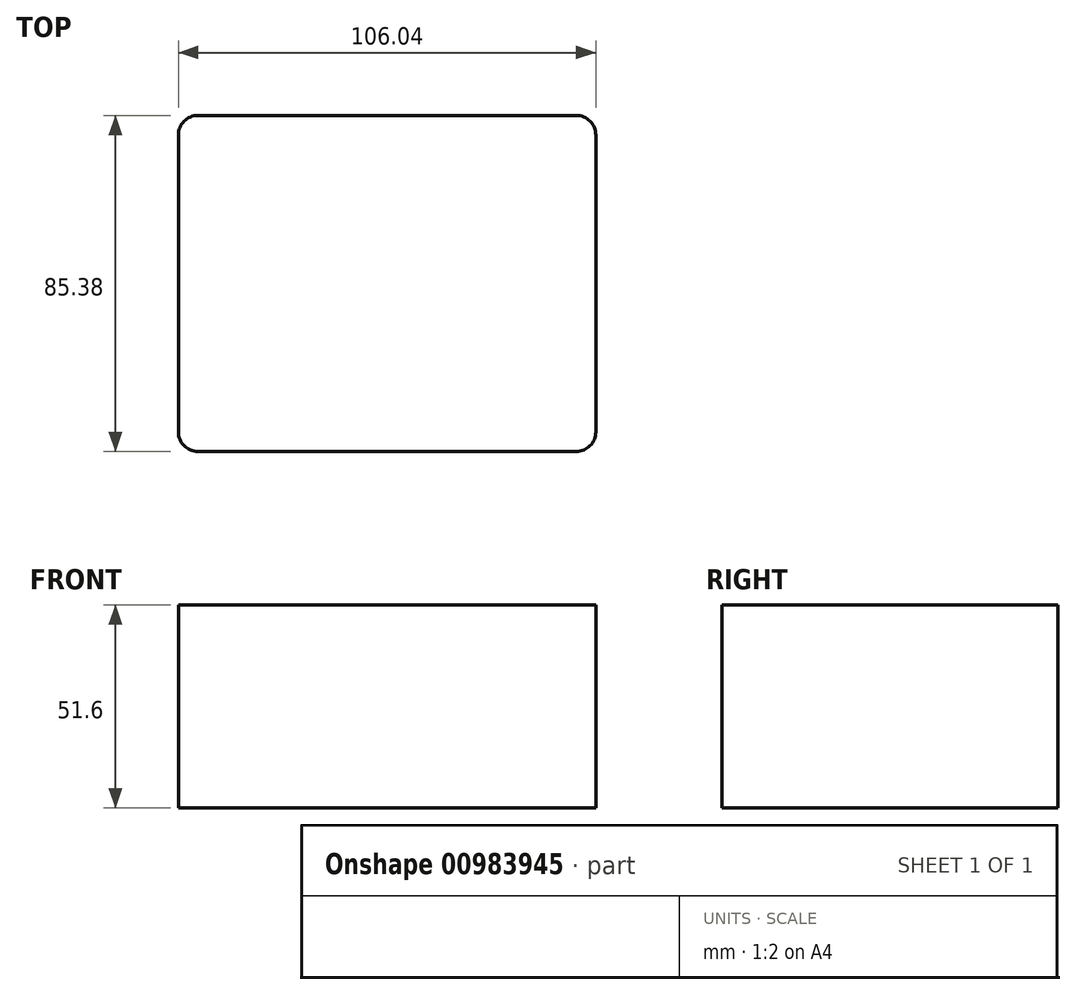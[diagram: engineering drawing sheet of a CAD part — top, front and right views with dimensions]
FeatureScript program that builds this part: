
annotation { "Feature Type Name" : "Feature", "Feature Type Description" : "" }
export const myFeature = defineFeature(function(context is Context, id is Id, definition is map)
    precondition{}
    {
        {
            var Q0;
            Q0=qCreatedBy(makeId("Top.planeOp"),FACE);
            var sketch = newSketch(context, id + "F0", { "sketchPlane" : qUnion([Q0])});
            skLineSegment(sketch, "E0.bottom", {"start": v(-53.02, 42.7) * mm, "end": v(53.02, 42.7) * mm});
            skLineSegment(sketch, "E0.top", {"start": v(-53.02, -42.7) * mm, "end": v(53.02, -42.7) * mm});
            skLineSegment(sketch, "E0.left", {"start": v(-53.02, 42.7) * mm, "end": v(-53.02, -42.7) * mm});
            skLineSegment(sketch, "E0.right", {"start": v(53.02, 42.7) * mm, "end": v(53.02, -42.7) * mm});
            skPoint(sketch, "E1", {"position": v(0, 42.7) * mm});
            skPoint(sketch, "E2", {"position": v(-53.02, 0) * mm});
            skSolve(sketch);
        }
        {
            var Q0;
            Q0=makeQuery(id+"F0.imprint","IMPRINT",FACE,{"disambiguationData":[TD([[makeQuery(id+"F0.imprint","IMPRINT",EDGE,{"derivedFrom":sQuery(id+"F0.wireOp",EDGE,"E0.bottom")}),-1.0]])]});
            extrude(context, id + "F1", {"entities" : qUnion([Q0]), "depth" : 51.6 * mm, "offsetDistance" : 25 * mm});
        }
        {
            var Q0;
            Q0=makeQuery(id+"F1.opExtrude","SWEPT_EDGE",EDGE,{"disambiguationData":[OSD([sQuery(id+"F0.wireOp",EDGE,"E0.bottom"),sQuery(id+"F0.wireOp",EDGE,"E0.right")])]});
            var Q1;
            Q1=makeQuery(id+"F1.opExtrude","SWEPT_EDGE",EDGE,{"disambiguationData":[OSD([sQuery(id+"F0.wireOp",EDGE,"E0.bottom"),sQuery(id+"F0.wireOp",EDGE,"E0.left")])]});
            var Q2;
            Q2=makeQuery(id+"F1.opExtrude","SWEPT_EDGE",EDGE,{"disambiguationData":[OSD([sQuery(id+"F0.wireOp",EDGE,"E0.top"),sQuery(id+"F0.wireOp",EDGE,"E0.left")])]});
            var Q3;
            Q3=makeQuery(id+"F1.opExtrude","SWEPT_EDGE",EDGE,{"disambiguationData":[OSD([sQuery(id+"F0.wireOp",EDGE,"E0.top"),sQuery(id+"F0.wireOp",EDGE,"E0.right")])]});
            fillet(context, id + "F2", {"entities" : qUnion([Q0, Q1, Q2, Q3]), "radius" : 5 * mm, "tangentPropagation" : true, "allowEdgeOverflow" : false});
        }
    });
